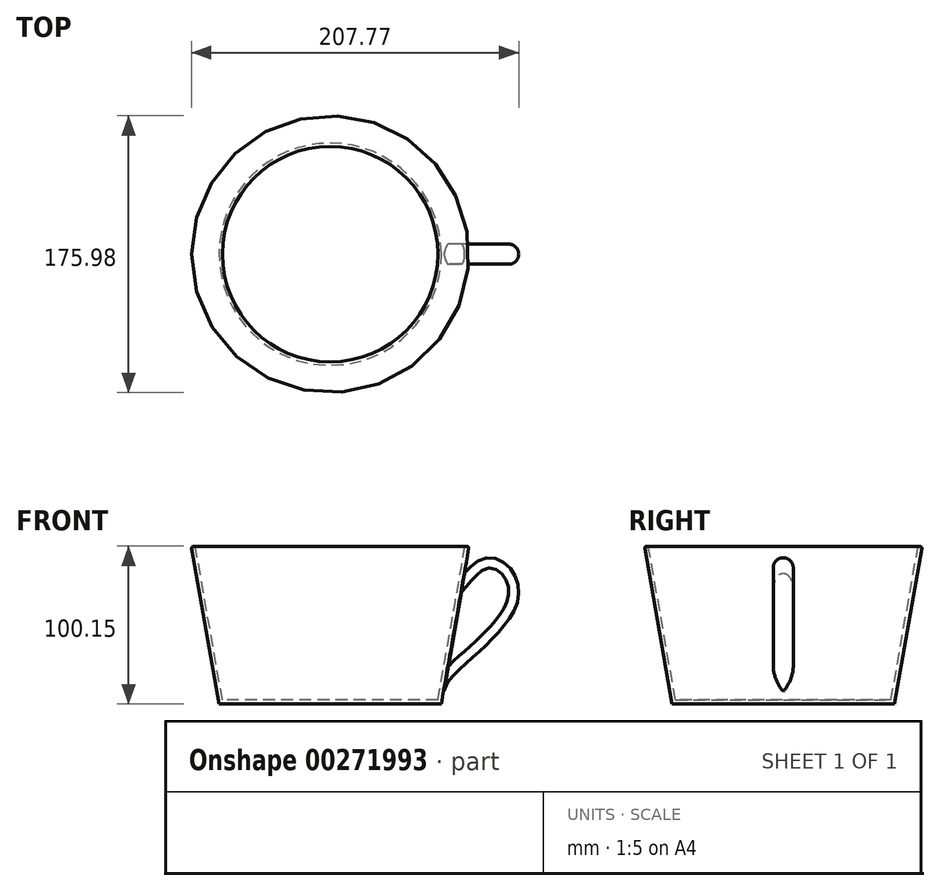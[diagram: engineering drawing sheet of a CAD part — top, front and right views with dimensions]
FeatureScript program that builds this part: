
annotation { "Feature Type Name" : "Feature", "Feature Type Description" : "" }
export const myFeature = defineFeature(function(context is Context, id is Id, definition is map)
    precondition{}
    {
        {
            var Q0;
            Q0=qCreatedBy(makeId("Top.planeOp"),FACE);
            var sketch = newSketch(context, id + "F0", { "sketchPlane" : qUnion([Q0])});
            skCircle(sketch, "E0", {"center": v(0, 0) * mm, "radius": 70.58 * mm});
            skSolve(sketch);
        }
        {
            var Q0;
            Q0 = qSketchRegion(id + "F0", true);
            extrude(context, id + "F1", {"entities" : qUnion([Q0]), "depth" : 101.6 * mm, "hasDraft" : true, "draftAngle" : 10 * degree});
        }
        {
            var Q0;
            Q0=makeQuery(id+"F1.opExtrude","CAP_FACE",FACE,{"disambiguationData":[OSD([sQuery(id+"F0.wireOp",EDGE,"E0")])],"isStart":false});
            shell(context, id + "F2", {"entities" : qUnion([Q0]), "thickness" : 2.54 * mm});
        }
        {
            var Q0;
            Q0=qCreatedBy(makeId("Front.planeOp"),FACE);
            var sketch = newSketch(context, id + "F3", { "sketchPlane" : qUnion([Q0])});
            skFitSpline(sketch, "E1", {"points": [v(85.39, 83.05) * mm, v(97.28, 92.21) * mm, v(111.58, 88.85) * mm, v(118.32, 62.76) * mm, v(78.35, 18.17) * mm, v(72.34, 8.16) * mm], "startDerivative": vector(65.28, 73.49) * mm, "endDerivative": vector(-16.7, -60.38) * mm});
            skLineSegment(sketch, "E2", {"start": v(85.39, 83.05) * mm, "end": v(72.34, 8.16) * mm});
            skFitSpline(sketch, "E3.0", {"points": [v(90.13, 78.83) * mm, v(90.78, 79.56) * mm, v(92.06, 80.97) * mm, v(93.94, 82.84) * mm, v(95.44, 84.1) * mm, v(96.59, 84.9) * mm, v(97.4, 85.4) * mm, v(98.18, 85.8) * mm, v(98.8, 86.04) * mm, v(99.26, 86.18) * mm, v(99.74, 86.3) * mm, v(100.35, 86.41) * mm, v(101.12, 86.46) * mm, v(102.17, 86.43) * mm, v(103.55, 86.19) * mm, v(105, 85.63) * mm, v(106.17, 84.97) * mm, v(107.06, 84.35) * mm, v(107.96, 83.61) * mm, v(108.84, 82.74) * mm, v(109.7, 81.73) * mm, v(110.78, 80.25) * mm, v(111.96, 78.14) * mm, v(112.97, 75.3) * mm, v(113.4, 72.75) * mm, v(113.45, 70.61) * mm, v(113.33, 68.96) * mm, v(113.04, 67.25) * mm, v(112.65, 65.78) * mm, v(112.23, 64.59) * mm, v(111.73, 63.34) * mm, v(110.94, 61.7) * mm, v(109.76, 59.63) * mm, v(107.9, 56.77) * mm, v(105.07, 53.06) * mm, v(101.06, 48.51) * mm, v(95.17, 42.47) * mm, v(88.86, 36.63) * mm, v(82.87, 31.23) * mm, v(79.41, 28.09) * mm, v(76.9, 25.71) * mm, v(75.44, 24.3) * mm, v(74.35, 23.18) * mm, v(73.31, 22.09) * mm, v(72.13, 20.77) * mm, v(70.9, 19.24) * mm, v(69.46, 17.27) * mm, v(68.05, 14.89) * mm, v(66.9, 12.17) * mm, v(66.43, 10.58) * mm, v(66.22, 9.85) * mm]});
            skLineSegment(sketch, "E4", {"start": v(90.33, 79.05) * mm, "end": v(82.56, 66.82) * mm});
            skLineSegment(sketch, "E5", {"start": v(72.34, 8.16) * mm, "end": v(85.39, 83.05) * mm});
            skSolve(sketch);
        }
        {
            var Q0;
            Q0=makeQuery(id+"F3.imprint","IMPRINT",FACE,{"disambiguationData":[TD([[makeQuery(id+"F3.imprint","IMPRINT",EDGE,{"derivedFrom":sQuery(id+"F3.wireOp",EDGE,"E1")}),-1.0]])]});
            extrude(context, id + "F4", {"entities" : qUnion([Q0]), "endBound" : BoundingType.SYMMETRIC, "depth" : 12.7 * mm});
        }
        {
            var Q0;
            Q0=makeQuery(id+"F4.opExtrude","CAP_EDGE",EDGE,{"disambiguationData":[OSD([sQuery(id+"F3.wireOp",EDGE,"E1")])],"isStart":false});
            var Q1;
            Q1=makeQuery(id+"F4.opExtrude","CAP_EDGE",EDGE,{"disambiguationData":[OSD([sQuery(id+"F3.wireOp",EDGE,"E1")])],"isStart":true});
            fillet(context, id + "F5", {"entities" : qUnion([Q0, Q1]), "radius" : 6.35 * mm, "tangentPropagation" : true, "allowEdgeOverflow" : false});
        }
        {
            var Q0;
            Q0=makeQuery(id+"F1.opExtrude","CAP_EDGE",EDGE,{"disambiguationData":[OSD([sQuery(id+"F0.wireOp",EDGE,"E0")])],"isStart":false});
            fillet(context, id + "F6", {"entities" : qUnion([Q0]), "radius" : 2.54 * mm, "tangentPropagation" : true, "allowEdgeOverflow" : false});
        }
        {
            var Q0;
            {var subQ0=sQuery(id+"F0.wireOp",EDGE,"E0");Q0=makeQuery(id+"F6.opFillet","BLEND_EDGE",EDGE,{"blendedFrom":[makeQuery(id+"F1.opExtrude","CAP_EDGE",EDGE,{"disambiguationData":[OSD([subQ0])],"isStart":false}),makeQuery(id+"F2.opShell","OFFSET_FACE",FACE,{"disambiguationData":[OSD([subQ0]),TDD([makeQuery(id+"F1.opExtrude","SWEPT_FACE",FACE,{"disambiguationData":[OSD([subQ0])]})])]})],"blendedInto":[makeQuery(id+"F2.opShell","OFFSET_FACE",FACE,{"disambiguationData":[OSD([subQ0]),TDD([makeQuery(id+"F1.opExtrude","SWEPT_FACE",FACE,{"disambiguationData":[OSD([subQ0])]})])]})]});}
            fillet(context, id + "F7", {"entities" : qUnion([Q0]), "radius" : 1.27 * mm, "tangentPropagation" : true, "allowEdgeOverflow" : false});
        }
    });
